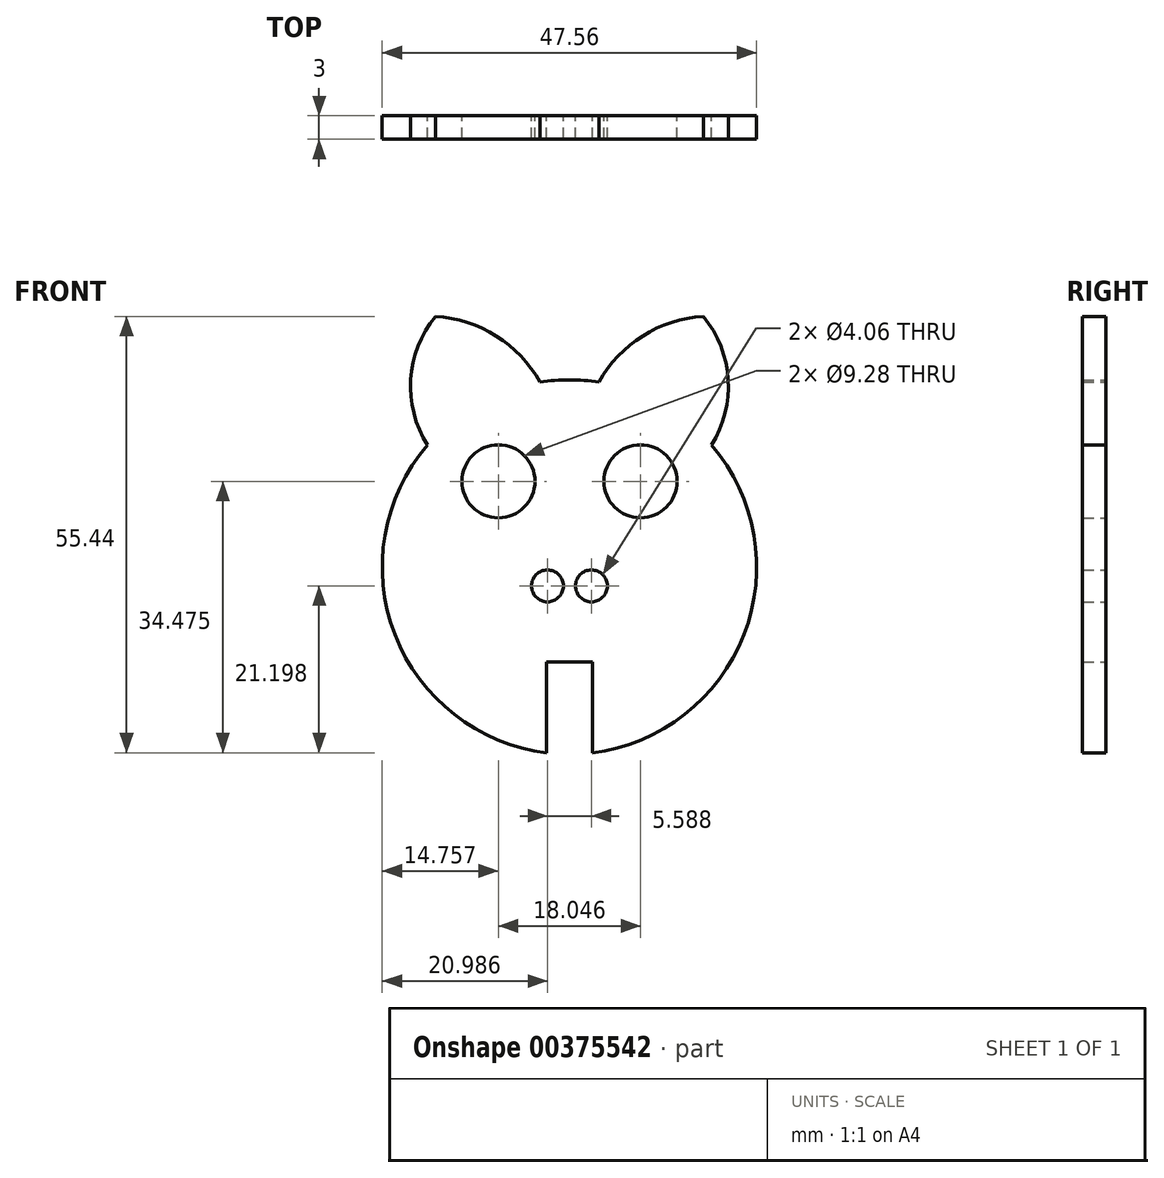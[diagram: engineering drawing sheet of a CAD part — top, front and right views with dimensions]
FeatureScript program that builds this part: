
annotation { "Feature Type Name" : "Feature", "Feature Type Description" : "" }
export const myFeature = defineFeature(function(context is Context, id is Id, definition is map)
    precondition{}
    {
        {
            var Q0;
            Q0=qCreatedBy(makeId("Front.planeOp"),FACE);
            var sketch = newSketch(context, id + "F0", { "sketchPlane" : qUnion([Q0])});
            skArc(sketch, "E0", {"start": v(2.9, -23.6) * mm, "mid": v(22.18, -8.58) * mm, "end": v(18.04, 15.5) * mm});
            skCircle(sketch, "E1", {"center": v(9.02, 10.88) * mm, "radius": 4.64 * mm});
            skCircle(sketch, "E2", {"center": v(2.8, -2.4) * mm, "radius": 2.03 * mm});
            skLineSegment(sketch, "E3.top", {"start": v(2.9, -12.07) * mm, "end": v(0, -12.07) * mm});
            skLineSegment(sketch, "E3.left", {"start": v(2.9, -23.6) * mm, "end": v(2.9, -12.07) * mm});
            skLineSegment(sketch, "E3.right", {"start": v(0, -23.6) * mm, "end": v(0, -12.07) * mm});
            skLineSegment(sketch, "E4", {"start": v(0, 23.78) * mm, "end": v(0, -23.6) * mm});
            skArc(sketch, "E5", {"start": v(17, 31.84) * mm, "mid": v(9.3, 29.35) * mm, "end": v(3.74, 23.48) * mm});
            skArc(sketch, "E6.trimOffspring", {"start": v(18.04, 15.5) * mm, "mid": v(20.16, 23.84) * mm, "end": v(17, 31.84) * mm});
            skArc(sketch, "E7.trimOffspring", {"start": v(3.74, 23.48) * mm, "mid": v(1.88, 23.7) * mm, "end": v(0, 23.78) * mm});
            skLineSegment(sketch, "E8.MirrorCS", {"start": v(-2.9, -12.07) * mm, "end": v(0, -12.07) * mm});
            skCircle(sketch, "E9.MirrorC", {"center": v(-9.02, 10.88) * mm, "radius": 4.64 * mm});
            skArc(sketch, "E10.MirrorCS", {"start": v(-18.04, 15.5) * mm, "mid": v(-20.16, 23.84) * mm, "end": v(-17, 31.84) * mm});
            skLineSegment(sketch, "E11.MirrorCS", {"start": v(-2.9, -23.6) * mm, "end": v(-2.9, -12.07) * mm});
            skArc(sketch, "E12.MirrorCS", {"start": v(-17, 31.84) * mm, "mid": v(-9.3, 29.35) * mm, "end": v(-3.74, 23.48) * mm});
            skArc(sketch, "E13.MirrorCS", {"start": v(-3.74, 23.48) * mm, "mid": v(-1.88, 23.7) * mm, "end": v(0, 23.78) * mm});
            skArc(sketch, "E14.MirrorCS", {"start": v(-2.9, -23.6) * mm, "mid": v(-22.18, -8.58) * mm, "end": v(-18.04, 15.5) * mm});
            skCircle(sketch, "E15.MirrorC", {"center": v(-2.8, -2.4) * mm, "radius": 2.03 * mm});
            skSolve(sketch);
        }
        {
            var Q0;
            Q0 = qSketchRegion(id + "F0", true);
            extrude(context, id + "F1", {"entities" : qUnion([Q0]), "depth" : 3 * mm});
        }
    });
